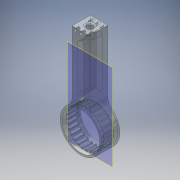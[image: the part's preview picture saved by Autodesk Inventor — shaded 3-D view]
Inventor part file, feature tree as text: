
AUTODESK INVENTOR PART (.ipt)
format: ipt  version: 2019.4 (Build 234330000, 330)  size: 850,944 bytes
history: native  units: mm
features: sketch x8, extrude x7, fillet x5, mirror x2, pattern_circular x1, plane x1, hole x1, pattern_linear x1, other x1, projected_geometry x1
ambient origin geometry x8: Origin, YZ Plane, XZ Plane, XY Plane, X Axis, Y Axis, Z Axis, Center Point
bodies: Body1 (feature_tree)
feature tree (28):
  extrude  "Extrusion4"  Depth=8.0mm
  extrude  "Extrusion5"  Depth=80.0mm TaperAngle=360.0deg
  fillet  "Fillet1"  Radius=27.0mm
  pattern_circular  "Circular Pattern3"  Count=5  [1 undecoded]
  extrude  "Extrusion6"  Depth=3.0mm
  extrude  "Extrusion7"  Depth=3.0mm
  extrude  "Extrusion8"  TaperAngle=360.0deg  [1 undecoded]
  fillet  "Fillet2"  Radius=65.0mm
  extrude  "Extrusion10"  Depth=3.0mm TaperAngle=0.0deg
  fillet  "Fillet4"  Radius=65.0mm
  fillet  "Fillet5"  Radius=7.0mm
  plane  "Work Plane1"
  mirror  "Mirror1"
  hole  "Hole1"  [1 undecoded]
  pattern_linear  "Rectangular Pattern1"  Count1=3  [1 undecoded]
  mirror  "Mirror2"
  extrude  "Extrusion11"  Depth=10.0mm TaperAngle=0.0deg
  fillet  "Fillet6"  Radius=20.0mm
  sketch  "Sketch1"  dims[d0=0.0mm d1=3600.0mm d2=8.0mm]
  other  "2D Equation Curve1"
  sketch  "Sketch4"  dims[d3=23.5mm d5=80.0mm d7=360.0deg d9=27.0mm]
  sketch  "Sketch5"  dims[d18=0.581776mm]
  sketch  "Sketch6"  dims[d25=65.0mm]
  sketch  "Sketch8"  dims[d28=3.5mm]
  sketch  "Sketch11"  dims[d29=17.5mm d30=0.0mm]
  sketch  "Sketch12"  dims[d31=3.0mm]
  sketch  "Sketch13"  dims[d32=31.65mm d33=50.0mm d34=0.0mm d35=1.5mm d36=270.0mm d37=360.0deg d39=65.0mm d40=7.0mm d41=0.0mm d42=65.0mm d43=7.0mm d44=0.0mm d45=70.0mm d46=30.0mm d47=10.0mm d48=0.0mm d53=20.0mm d55=150.0mm d56=15.0mm d57=10.0mm d58=10.0mm d59=45.0mm d60=10.0mm d61=0.0mm d62=4.0mm d63=0.8mm d64=3.0mm d65=4.0mm d66=3.88mm d67=6.0mm d68=4.34mm d69=2.0mm d70=1.22173mm d71=7.0mm d72=0.0mm d73=20.0mm d75=10.0mm d76=20.0mm d78=10.0mm d79=10.0mm d80=30.0mm d81=0.0mm d82=3.0mm d83=3.0mm d74=20.594885mm d77=0.375mm]
  projected_geometry  "Projected Loop3"
note: 4 required parameter values undecoded (feature->parameter linkage not recoverable at this tier; creation-order binding heuristic only, values carry confidence <= 0.55)
